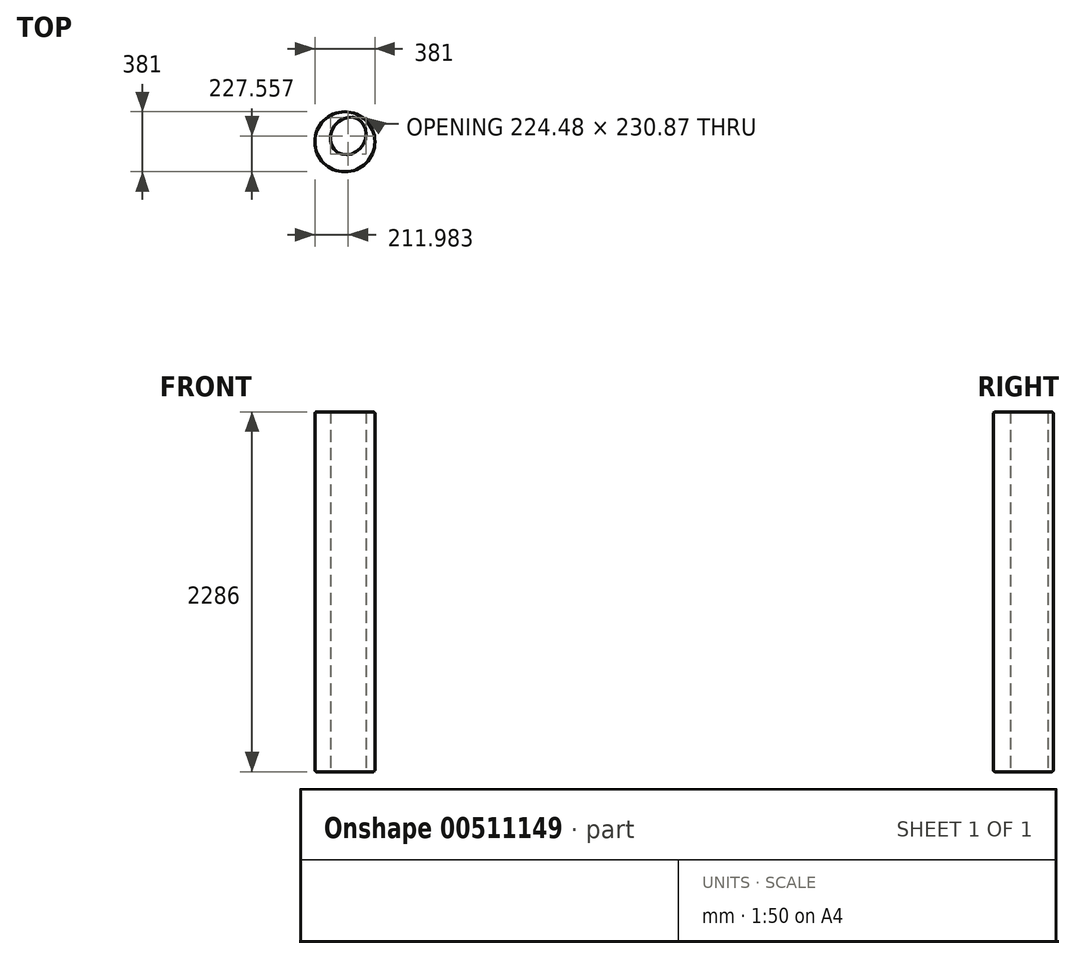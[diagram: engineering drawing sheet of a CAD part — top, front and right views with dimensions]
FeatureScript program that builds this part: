
annotation { "Feature Type Name" : "Feature", "Feature Type Description" : "" }
export const myFeature = defineFeature(function(context is Context, id is Id, definition is map)
    precondition{}
    {
        {
            var Q0;
            Q0=qCreatedBy(makeId("Top.planeOp"),FACE);
            var sketch = newSketch(context, id + "F0", { "sketchPlane" : qUnion([Q0])});
            skCircle(sketch, "E0", {"center": v(0, 0) * mm, "radius": 190.5 * mm});
            skSolve(sketch);
        }
        {
            var Q0;
            Q0 = qSketchRegion(id + "F0", true);
            extrude(context, id + "F1", {"entities" : qUnion([Q0]), "depth" : 2286 * mm});
        }
        {
            var Q0;
            Q0=makeQuery(id+"F1.opExtrude","CAP_FACE",FACE,{"disambiguationData":[OSD([sQuery(id+"F0.wireOp",EDGE,"E0")])],"isStart":false});
            var sketch = newSketch(context, id + "F2", { "sketchPlane" : qUnion([Q0])});
            skEllipse(sketch, "E1", {"center": v(21.48, 37.06) * mm, "majorRadius": 124.07 * mm, "minorRadius": 108.71 * mm, "majorAxis": v(-0.54, -0.84)});
            skSolve(sketch);
        }
        {
            var Q0;
            Q0=makeQuery(id+"F2.imprint","IMPRINT",FACE,{"disambiguationData":[TD([[makeQuery(id+"F2.imprint","IMPRINT",EDGE,{"derivedFrom":sQuery(id+"F2.wireOp",EDGE,"E1")}),1.0]])]});
            var Q1;
            Q1=sQuery(id+"F2.wireOp",EDGE,"E1");
            extrude(context, id + "F3", {"entities" : qUnion([Q0]), "operationType" : NewBodyOperationType.REMOVE, "surfaceEntities" : qUnion([Q1]), "oppositeDirection" : true, "depth" : 4384.37 * mm});
        }
        {
            var Q0;
            Q0=makeQuery(id+"F1.opExtrude","CAP_EDGE",EDGE,{"disambiguationData":[OSD([sQuery(id+"F0.wireOp",EDGE,"E0")])],"isStart":false});
            var Q1;
            Q1=makeQuery(id+"F3.boolean.opBoolean","COPY",EDGE,{"derivedFrom":makeQuery(id+"F3.opExtrude","CAP_EDGE",EDGE,{"disambiguationData":[OSD([sQuery(id+"F2.wireOp",EDGE,"E1")])],"isStart":true})});
            var Q2;
            Q2=makeQuery(id+"F1.opExtrude","CAP_EDGE",EDGE,{"disambiguationData":[OSD([sQuery(id+"F0.wireOp",EDGE,"E0")])],"isStart":true});
            fillet(context, id + "F4", {"entities" : qUnion([Q0, Q1, Q2]), "radius" : 12.7 * mm, "tangentPropagation" : true, "allowEdgeOverflow" : false});
        }
    });
